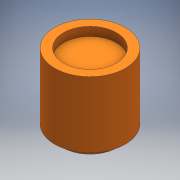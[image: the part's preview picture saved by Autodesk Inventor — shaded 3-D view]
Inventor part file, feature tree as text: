
AUTODESK INVENTOR PART (.ipt)
format: ipt  version: 2016 (Build 200138000, 138)  size: 123,904 bytes
history: native  units: mm
features: extrude x3, sketch x3
ambient origin geometry x8: Origin, YZ Plane, XZ Plane, XY Plane, X Axis, Y Axis, Z Axis, Center Point
bodies: Solid1 (feature_tree)
feature tree (6):
  extrude  "Extrusion1"  Depth=6.0mm
  extrude  "Extrusion2"  Depth=56.0mm TaperAngle=0.0deg
  extrude  "Extrusion3"  Depth=7.5mm TaperAngle=0.0deg
  sketch  "Sketch1"  dims[d0=46.0mm d1=6.0mm d2=-3.490659mm]
  sketch  "Sketch2"  dims[d3=60.0mm d4=56.0mm d5=0.0mm]
  sketch  "Sketch3"  dims[d6=45.0mm d7=7.5mm d8=0.0mm]
